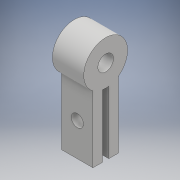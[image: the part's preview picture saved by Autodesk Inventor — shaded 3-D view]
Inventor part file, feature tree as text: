
AUTODESK INVENTOR PART (.ipt)
format: ipt  version: 2017 (Build 210142000, 142)  size: 124,416 bytes
history: native  units: mm
features: extrude x2, sketch x2
ambient origin geometry x8: Origin, YZ Plane, XZ Plane, XY Plane, X Axis, Y Axis, Z Axis, Center Point
bodies: Solid1 (feature_tree)
feature tree (4):
  extrude  "Extrusion1"  Depth=2.5mm
  extrude  "Extrusion3"  Depth=10.0mm
  sketch  "Sketch1"  dims[d0=7.0mm d1=2.5mm]
  sketch  "Sketch3"  dims[d2=0.5mm d3=10.0mm d4=5.0mm d5=0.0mm d10=10.0mm d11=0.0mm]
